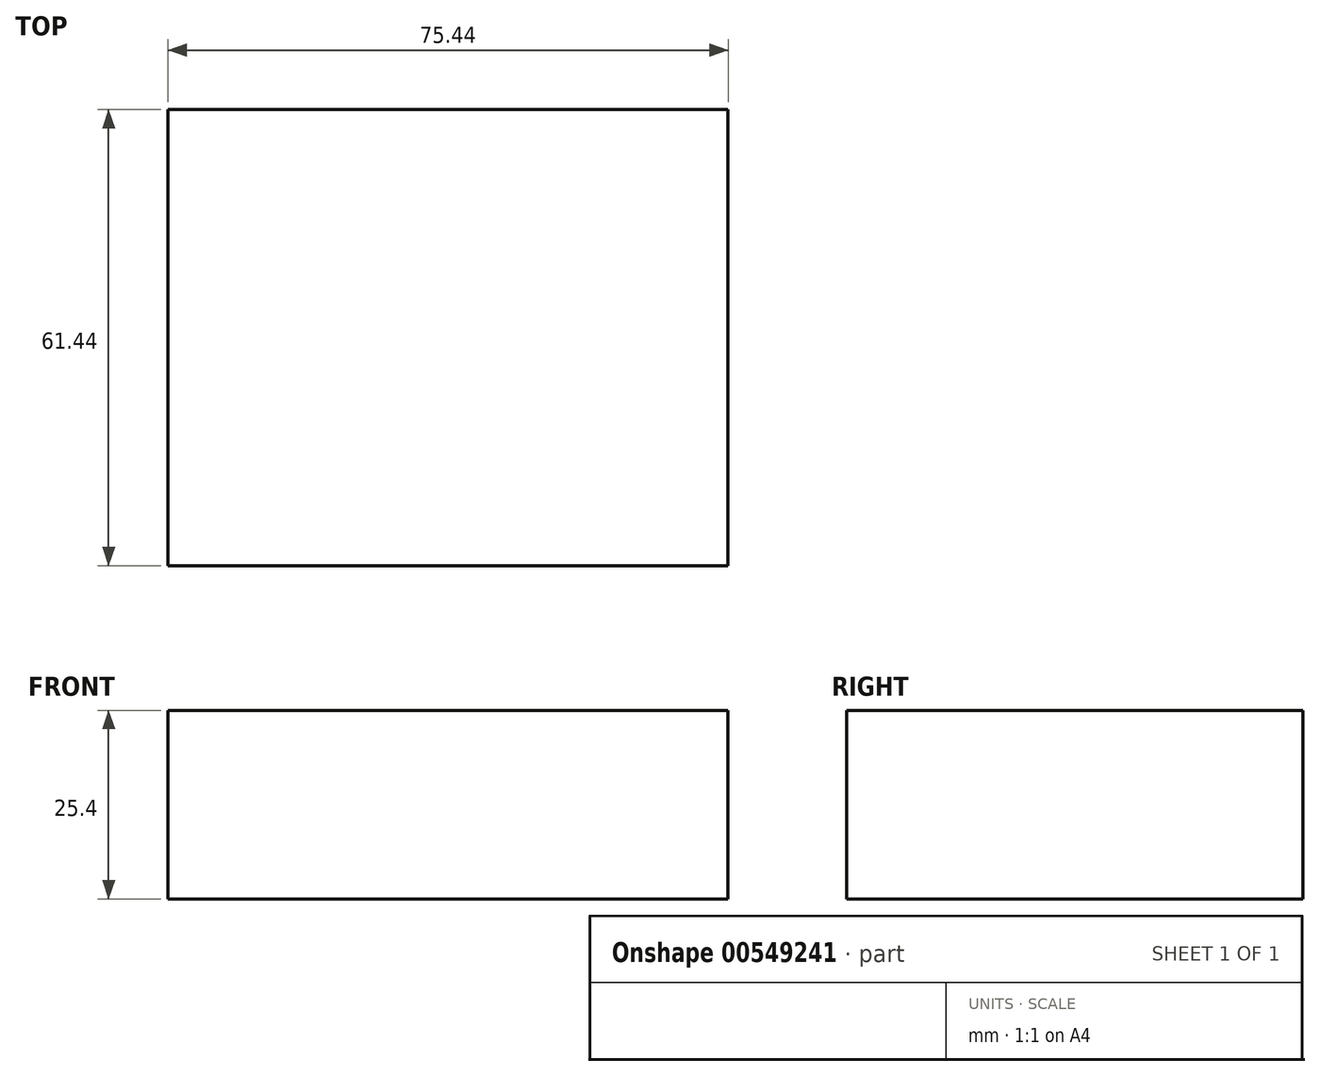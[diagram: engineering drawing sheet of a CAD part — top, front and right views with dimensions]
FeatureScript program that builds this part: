
annotation { "Feature Type Name" : "Feature", "Feature Type Description" : "" }
export const myFeature = defineFeature(function(context is Context, id is Id, definition is map)
    precondition{}
    {
        {
            var Q0;
            Q0=qCreatedBy(makeId("Top.planeOp"),FACE);
            var sketch = newSketch(context, id + "F0", { "sketchPlane" : qUnion([Q0])});
            skLineSegment(sketch, "E0.bottom", {"start": v(-39.35, 25.79) * mm, "end": v(36.09, 25.79) * mm});
            skLineSegment(sketch, "E0.top", {"start": v(-39.35, -35.65) * mm, "end": v(36.09, -35.65) * mm});
            skLineSegment(sketch, "E0.left", {"start": v(-39.35, 25.79) * mm, "end": v(-39.35, -35.65) * mm});
            skLineSegment(sketch, "E0.right", {"start": v(36.09, 25.79) * mm, "end": v(36.09, -35.65) * mm});
            skSolve(sketch);
        }
        {
            var Q0;
            Q0=sQuery(id+"F0.wireOp",EDGE,"E0.left");
            var Q1;
            Q1=sQuery(id+"F0.wireOp",EDGE,"E0.top");
            var Q2;
            Q2=sQuery(id+"F0.wireOp",EDGE,"E0.right");
            var Q3;
            Q3=sQuery(id+"F0.wireOp",EDGE,"E0.bottom");
            extrude(context, id + "F1", {"bodyType" : ToolBodyType.SURFACE, "surfaceEntities" : qUnion([Q0, Q1, Q2, Q3]), "depth" : 25.4 * mm, "offsetDistance" : 25.4 * mm});
        }
    });
